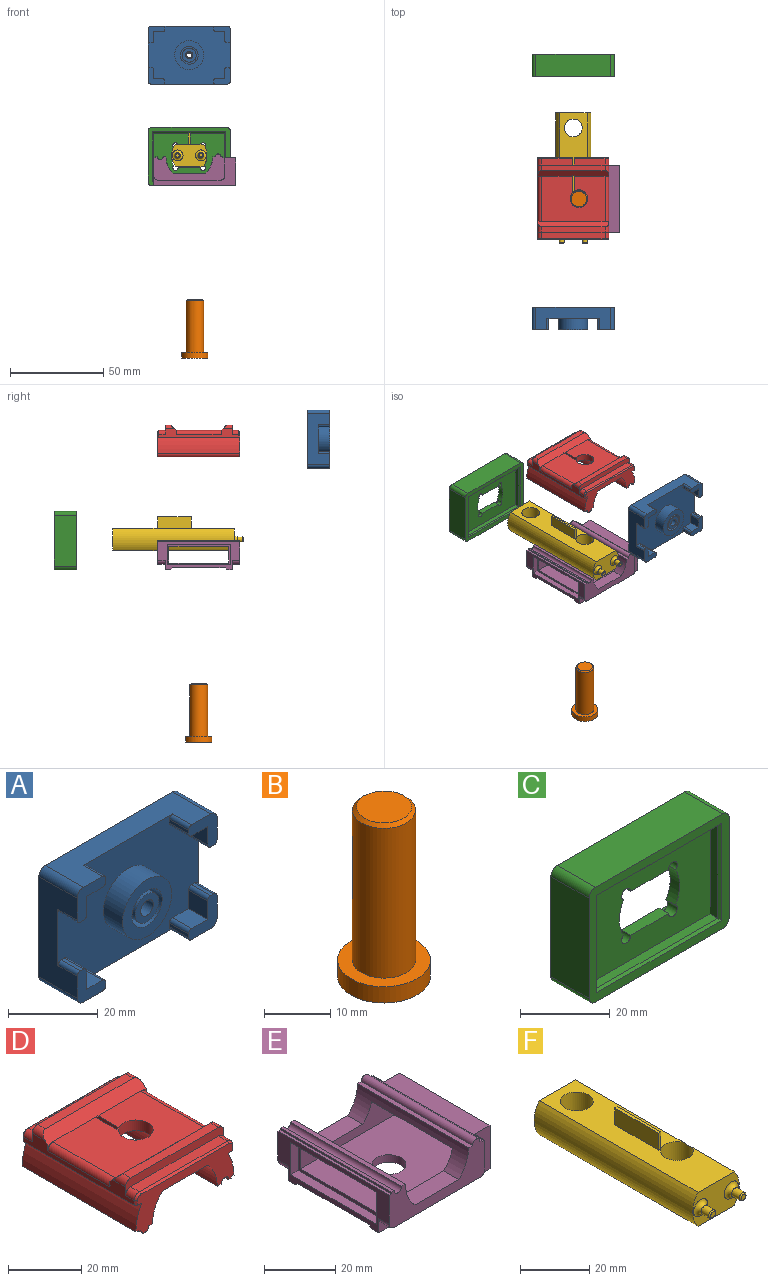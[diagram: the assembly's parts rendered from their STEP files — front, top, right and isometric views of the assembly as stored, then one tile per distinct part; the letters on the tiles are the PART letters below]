
ASSEMBLY  parts=6 mates=4
PART A: 69 faces, bbox 44.1x12x31.3 mm
  f0: plane 9.5x9.5mm, normal (0,-1,0), area 26.7mm2, adj f17,f39
  f1: plane 44.1x31.3mm, normal (0,-1,0), area 1015.1mm2, adj f10,f11,f12,f13,f19,f20,f21,f22
  f2: cylinder r=1.4mm len=2.8mm, axis (0,-1,0), area 17.6mm2, adj f5,f16
  f3: cylinder r=1.4mm len=2.8mm, axis (0,-1,0), area 17.6mm2, adj f5,f15
  f4: cylinder r=2mm len=6mm, axis (0,-1,0), area 75.4mm2, adj f18,f47
  f5: plane 38.1x25.3mm, normal (0,1,0), area 945.5mm2, adj f2,f3,f6,f7,f8,f9,f46
  f6: plane 25.3x2.4mm, normal (-1,0,0), area 60.7mm2, adj f5,f7,f9,f44
  f7: plane 38.1x2.4mm, normal (0,0,-1), area 91.4mm2, adj f5,f6,f8,f42
  f8: plane 25.3x2.4mm, normal (1,0,0), area 60.7mm2, adj f5,f7,f9,f43
  f9: plane 38.1x2.4mm, normal (0,0,1), area 91.4mm2, adj f5,f6,f8,f45
  f10: plane 27.3x12mm, normal (-1,0,0), area 235.8mm2, adj f1,f14,f28,f33,f48,f50,f58,f68
  f11: plane 40.1x12mm, normal (0,0,-1), area 312.6mm2, adj f1,f14,f33,f38,f50,f51,f55,f57
  f12: plane 27.3x12mm, normal (1,0,0), area 235.8mm2, adj f1,f14,f23,f38,f49,f51,f54,f64
  f13: plane 40.1x12mm, normal (0,0,1), area 312.6mm2, adj f1,f14,f23,f28,f48,f49,f61,f65
  f14: plane 44.1x31.3mm, normal (0,1,0), area 335.4mm2, adj f10,f11,f12,f13,f42,f43,f44,f45
  f15: plane 2.8x2.8mm, normal (0,1,0), area 6.2mm2, adj f3
  f16: plane 2.8x2.8mm, normal (0,1,0), area 6.2mm2, adj f2
  f17: cylinder r=3.75mm len=7.5mm, axis (0,1,0), area 141.4mm2, adj f0,f18
  f18: plane 7.5x7.5mm, normal (0,-1,0), area 31.6mm2, adj f4,f17
  f19: plane 6x1mm, normal (-1,0,0), area 6mm2, adj f1,f23,f61,f62
  f20: plane 6x5mm, normal (0,0,-1), area 30mm2, adj f1,f21,f23,f62
  f21: plane 6x5mm, normal (-1,0,0), area 30mm2, adj f1,f20,f23,f63
  f22: plane 6x1mm, normal (0,0,-1), area 6mm2, adj f1,f23,f63,f64
  f23: plane 9x9mm, normal (0,-1,0), area 43.3mm2, adj f12,f13,f19,f20,f21,f22,f49,f61
  f24: plane 6x1mm, normal (0,0,-1), area 6mm2, adj f1,f28,f67,f68
  f25: plane 6x5mm, normal (1,0,0), area 30mm2, adj f1,f26,f28,f67
  f26: plane 6x5mm, normal (0,0,-1), area 30mm2, adj f1,f25,f28,f66
  f27: plane 6x1mm, normal (1,0,0), area 6mm2, adj f1,f28,f65,f66
  f28: plane 9x9mm, normal (0,-1,0), area 43.3mm2, adj f10,f13,f24,f25,f26,f27,f48,f65
  f29: plane 6x1mm, normal (1,0,0), area 6mm2, adj f1,f33,f57,f60
  f30: plane 6x5mm, normal (0,0,1), area 30mm2, adj f1,f31,f33,f60
  f31: plane 6x5mm, normal (1,0,0), area 30mm2, adj f1,f30,f33,f59
  f32: plane 6x1mm, normal (0,0,1), area 6mm2, adj f1,f33,f58,f59
  f33: plane 9x9mm, normal (0,-1,0), area 43.3mm2, adj f10,f11,f29,f30,f31,f32,f50,f57
  f34: plane 6x5mm, normal (0,0,1), area 30mm2, adj f1,f37,f38,f56
  f35: plane 6x1mm, normal (-1,0,0), area 6mm2, adj f1,f38,f55,f56
  f36: plane 6x1mm, normal (0,0,1), area 6mm2, adj f1,f38,f53,f54
  f37: plane 6x5mm, normal (-1,0,0), area 30mm2, adj f1,f34,f38,f53
  f38: plane 9x9mm, normal (0,-1,0), area 43.3mm2, adj f11,f12,f34,f35,f36,f37,f51,f53
  f39: cylinder r=4.75mm len=9.5mm, axis (0,1,0), area 179.1mm2, adj f0,f41
  f40: cylinder r=7.75mm len=15.5mm, axis (0,1,0), area 292.2mm2, adj f1,f41
  f41: plane 15.5x15.5mm, normal (0,-1,0), area 117.8mm2, adj f39,f40
  f42: plane 39.3x0.6mm, normal (0,0.71,-0.71), area 32.8mm2, adj f7,f14,f43,f44
  f43: plane 26.5x0.6mm, normal (0.71,0.71,0), area 22mm2, adj f8,f14,f42,f45
  f44: plane 26.5x0.6mm, normal (-0.71,0.71,0), area 22mm2, adj f6,f14,f42,f45
  f45: plane 39.3x0.6mm, normal (0,0.71,0.71), area 32.8mm2, adj f9,f14,f43,f44
  f46: cylinder r=1.4mm len=2.8mm, axis (0,-1,0), area 22.9mm2, adj f5,f52
  f47: plane 4x4mm, normal (0,-1,0), area 2.4mm2, adj f4,f52
  f48: cylinder r=2mm len=12mm, axis (0,1,0), area 37.7mm2, adj f10,f13,f14,f28
  f49: cylinder r=2mm len=12mm, axis (0,-1,0), area 37.7mm2, adj f12,f13,f14,f23
  f50: cylinder r=2mm len=12mm, axis (0,-1,0), area 37.7mm2, adj f10,f11,f14,f33
  f51: cylinder r=2mm len=12mm, axis (0,1,0), area 37.7mm2, adj f11,f12,f14,f38
  f52: cone r=1.4mm half-angle=45deg, axis (0,-1,0), area 5.7mm2, adj f46,f47
  f53: cylinder r=1mm len=6mm, axis (0,-1,0), area 9.4mm2, adj f1,f36,f37,f38
  f54: cylinder r=1mm len=6mm, axis (0,-1,0), area 9.4mm2, adj f1,f12,f36,f38
  f55: cylinder r=1mm len=6mm, axis (0,-1,0), area 9.4mm2, adj f1,f11,f35,f38
  f56: cylinder r=1mm len=6mm, axis (0,-1,0), area 9.4mm2, adj f1,f34,f35,f38
  f57: cylinder r=1mm len=6mm, axis (0,1,0), area 9.4mm2, adj f1,f11,f29,f33
  f58: cylinder r=1mm len=6mm, axis (0,1,0), area 9.4mm2, adj f1,f10,f32,f33
  f59: cylinder r=1mm len=6mm, axis (0,1,0), area 9.4mm2, adj f1,f31,f32,f33
  f60: cylinder r=1mm len=6mm, axis (0,1,0), area 9.4mm2, adj f1,f29,f30,f33
  f61: cylinder r=1mm len=6mm, axis (0,1,0), area 9.4mm2, adj f1,f13,f19,f23
  f62: cylinder r=1mm len=6mm, axis (0,1,0), area 9.4mm2, adj f1,f19,f20,f23
  f63: cylinder r=1mm len=6mm, axis (0,1,0), area 9.4mm2, adj f1,f21,f22,f23
  f64: cylinder r=1mm len=6mm, axis (0,1,0), area 9.4mm2, adj f1,f12,f22,f23
  f65: cylinder r=1mm len=6mm, axis (0,-1,0), area 9.4mm2, adj f1,f13,f27,f28
  f66: cylinder r=1mm len=6mm, axis (0,-1,0), area 9.4mm2, adj f1,f26,f27,f28
  f67: cylinder r=1mm len=6mm, axis (0,-1,0), area 9.4mm2, adj f1,f24,f25,f28
  f68: cylinder r=1mm len=6mm, axis (0,-1,0), area 9.4mm2, adj f1,f10,f24,f28
PART B: 6 faces, bbox 14x14x31.2 mm
  f0: cylinder r=4.75mm len=27.6mm, axis (0,0,-1), area 823.7mm2, adj f3,f5
  f1: plane 8.3x8.3mm, normal (0,0,1), area 54.1mm2, adj f5
  f2: cylinder r=7mm len=14mm, axis (0,0,-1), area 131.9mm2, adj f3,f4
  f3: plane 14x14mm, normal (0,0,1), area 83.1mm2, adj f0,f2
  f4: plane 14x14mm, normal (0,0,-1), area 153.9mm2, adj f2
  f5: cone r=4.15mm half-angle=45deg, axis (0,0,-1), area 23.7mm2, adj f0,f1
PART C: 32 faces, bbox 44.1x12x31.3 mm
  f0: plane 38.1x25.3mm, normal (0,1,0), area 736.2mm2, adj f1,f2,f3,f4,f5,f6,f7,f8
  f1: cylinder r=1.4mm len=3mm, axis (0,1,0), area 17.2mm2, adj f0,f2,f8,f9
  f2: plane 11.93x3mm, normal (0,0,-1), area 35.8mm2, adj f0,f1,f3,f9
  f3: cylinder r=1.4mm len=3mm, axis (0,1,0), area 17.2mm2, adj f0,f2,f4,f9
  f4: cylinder r=9.5mm len=9.7mm, axis (0,1,0), area 30.6mm2, adj f0,f3,f5,f9
  f5: cylinder r=1.4mm len=3mm, axis (0,1,0), area 17.2mm2, adj f0,f4,f6,f9
  f6: plane 11.93x3mm, normal (0,0,1), area 35.8mm2, adj f0,f5,f7,f9
  f7: cylinder r=1.4mm len=3mm, axis (0,1,0), area 17.2mm2, adj f0,f6,f8,f9
  f8: cylinder r=9.5mm len=9.7mm, axis (0,1,0), area 30.6mm2, adj f0,f1,f7,f9
  f9: plane 38.1x25.3mm, normal (0,-1,0), area 736.2mm2, adj f1,f2,f3,f4,f5,f6,f7,f8
  f10: plane 38.1x2.4mm, normal (0,0,-1), area 91.4mm2, adj f9,f11,f13,f25
  f11: plane 25.3x2.4mm, normal (1,0,0), area 60.7mm2, adj f9,f10,f12,f24
  f12: plane 38.1x2.4mm, normal (0,0,1), area 91.4mm2, adj f9,f11,f13,f26
  f13: plane 25.3x2.4mm, normal (-1,0,0), area 60.7mm2, adj f9,f10,f12,f27
  f14: plane 40.1x12mm, normal (0,0,1), area 481.2mm2, adj f18,f23,f28,f31
  f15: plane 27.3x12mm, normal (-1,0,0), area 327.6mm2, adj f18,f23,f28,f29
  f16: plane 40.1x12mm, normal (0,0,-1), area 481.2mm2, adj f18,f23,f29,f30
  f17: plane 27.3x12mm, normal (1,0,0), area 327.6mm2, adj f18,f23,f30,f31
  f18: plane 44.1x31.3mm, normal (0,-1,0), area 335.4mm2, adj f14,f15,f16,f17,f24,f25,f26,f27
  f19: plane 25.3x6mm, normal (1,0,0), area 151.8mm2, adj f0,f20,f22,f23
  f20: plane 38.1x6mm, normal (0,0,-1), area 228.6mm2, adj f0,f19,f21,f23
  f21: plane 25.3x6mm, normal (-1,0,0), area 151.8mm2, adj f0,f20,f22,f23
  f22: plane 38.1x6mm, normal (0,0,1), area 228.6mm2, adj f0,f19,f21,f23
  f23: plane 44.1x31.3mm, normal (0,1,0), area 413mm2, adj f14,f15,f16,f17,f19,f20,f21,f22
  f24: plane 26.5x0.6mm, normal (0.71,-0.71,0), area 22mm2, adj f11,f18,f25,f26
  f25: plane 39.3x0.6mm, normal (0,-0.71,-0.71), area 32.8mm2, adj f10,f18,f24,f27
  f26: plane 39.3x0.6mm, normal (0,-0.71,0.71), area 32.8mm2, adj f12,f18,f24,f27
  f27: plane 26.5x0.6mm, normal (-0.71,-0.71,0), area 22mm2, adj f13,f18,f25,f26
  f28: cylinder r=2mm len=12mm, axis (0,-1,0), area 37.7mm2, adj f14,f15,f18,f23
  f29: cylinder r=2mm len=12mm, axis (0,1,0), area 37.7mm2, adj f15,f16,f18,f23
  f30: cylinder r=2mm len=12mm, axis (0,-1,0), area 37.7mm2, adj f16,f17,f18,f23
  f31: cylinder r=2mm len=12mm, axis (0,1,0), area 37.7mm2, adj f14,f17,f18,f23
PART D: 62 faces, bbox 38x44x17 mm
  f0: plane 1.9x1.36mm, normal (0,1,0), area 0.7mm2, adj f18,f42,f61
  f1: plane 1.9x1.36mm, normal (0,-1,0), area 0.7mm2, adj f17,f41,f60
  f2: plane 16.5x3.4mm, normal (0,0,1), area 56.1mm2, adj f4,f36,f40,f49
  f3: plane 16.5x3.4mm, normal (0,0,1), area 56.1mm2, adj f5,f36,f39,f52
  f4: plane 18x3.6mm, normal (1,0,0), area 64.1mm2, adj f2,f6,f8,f30,f31,f35,f36,f49
  f5: plane 17.96x3.6mm, normal (-1,0,0), area 63.9mm2, adj f3,f6,f8,f9,f10,f35,f36,f52
  f6: plane 34x24.21mm, normal (0,0,1), area 744.1mm2, adj f4,f5,f10,f31,f41,f42,f60,f61
  f7: plane 34x3.4mm, normal (0,0,1), area 115.6mm2, adj f34,f47,f48,f57
  f8: plane 44x17.35mm, normal (0,0,-1), area 674.5mm2, adj f4,f5,f9,f10,f26,f27,f29,f30
  f9: plane 18.49x12mm, normal (0,1,0), area 111.8mm2, adj f5,f8,f11,f12,f13,f14,f15,f16
  f10: cylinder r=4.75mm len=9.5mm, axis (0,0,-1), area 107.3mm2, adj f5,f6,f8,f31
  f11: cylinder r=1.5mm len=44mm, axis (0,1,0), area 207.3mm2, adj f9,f12,f28,f29
  f12: plane 44x1mm, normal (0,0,-1), area 44mm2, adj f9,f11,f13,f29
  f13: plane 44x0.5mm, normal (1,0,0), area 22mm2, adj f9,f12,f14,f29
  f14: plane 44x0.99mm, normal (0,0,-1), area 43.7mm2, adj f9,f13,f15,f29
  f15: cylinder r=19mm len=44mm, axis (0,1,0), area 390.5mm2, adj f9,f14,f16,f29
  f16: plane 44x2.27mm, normal (0,0,-1), area 99.4mm2, adj f9,f15,f17,f29,f54,f55
  f17: plane 42.8x4.5mm, normal (1,0,0), area 102.4mm2, adj f1,f16,f32,f34,f36,f39,f41,f44
  f18: plane 42.8x4.5mm, normal (-1,0,0), area 102.4mm2, adj f0,f19,f34,f36,f38,f40,f42,f43
  f19: plane 44x2.27mm, normal (0,0,-1), area 99.4mm2, adj f18,f20,f29,f30,f51,f59
  f20: cylinder r=19mm len=44mm, axis (0,1,0), area 390.5mm2, adj f19,f21,f29,f30
  f21: plane 44x0.99mm, normal (0,0,-1), area 43.7mm2, adj f20,f22,f29,f30
  f22: plane 44x0.5mm, normal (-1,0,0), area 22mm2, adj f21,f23,f29,f30
  f23: plane 44x1mm, normal (0,0,-1), area 44mm2, adj f22,f24,f29,f30
  f24: cylinder r=1.5mm len=44mm, axis (0,1,0), area 207.3mm2, adj f23,f25,f29,f30
  f25: plane 44x1.5mm, normal (0,0,-1), area 66mm2, adj f24,f26,f29,f30
  f26: cylinder r=12.5mm len=44mm, axis (0,1,0), area 442.1mm2, adj f8,f25,f29,f30
  f27: cylinder r=12.5mm len=44mm, axis (0,1,0), area 442.1mm2, adj f8,f9,f28,f29
  f28: plane 44x1.5mm, normal (0,0,-1), area 66mm2, adj f9,f11,f27,f29
  f29: plane 37.99x13.5mm, normal (0,-1,0), area 233.8mm2, adj f8,f11,f12,f13,f14,f15,f16,f19
  f30: plane 18.49x13.5mm, normal (0,1,0), area 118.9mm2, adj f4,f8,f19,f20,f21,f22,f23,f24
  f31: plane 3.6x0.94mm, normal (0,1,0), area 3.4mm2, adj f4,f6,f8,f10
  f32: plane 1.9x1.36mm, normal (0,1,0), area 0.7mm2, adj f17,f41,f61
  f33: plane 34x3mm, normal (0,0,1), area 102mm2, adj f34,f45,f46,f61
  f34: plane 38x4.9mm, normal (0,-1,0), area 110.1mm2, adj f7,f17,f18,f33,f45,f46,f47,f48
  f35: plane 6x1mm, normal (0,0,-1), area 6mm2, adj f4,f5,f36,f60
  f36: plane 38x4.9mm, normal (0,1,0), area 110.2mm2, adj f2,f3,f4,f5,f17,f18,f35,f37
  f37: plane 34x3mm, normal (0,0,1), area 102mm2, adj f36,f43,f44,f60
  f38: plane 1.9x1.36mm, normal (0,-1,0), area 0.7mm2, adj f18,f42,f60
  f39: cylinder r=2mm len=3.4mm, axis (0,1,0), area 10.7mm2, adj f3,f17,f36,f53
  f40: cylinder r=2mm len=3.4mm, axis (0,-1,0), area 10.7mm2, adj f2,f18,f36,f50
  f41: cylinder r=2mm len=24.21mm, axis (0,1,0), area 75.5mm2, adj f1,f6,f17,f32,f60,f61
  f42: cylinder r=2mm len=24.21mm, axis (0,-1,0), area 75.5mm2, adj f0,f6,f18,f38,f60,f61
  f43: cylinder r=2mm len=5mm, axis (0,-1,0), area 11.7mm2, adj f18,f36,f37,f60
  f44: cylinder r=2mm len=5mm, axis (0,1,0), area 11.7mm2, adj f17,f36,f37,f60
  f45: cylinder r=2mm len=5mm, axis (0,-1,0), area 11.7mm2, adj f18,f33,f34,f61
  f46: cylinder r=2mm len=5mm, axis (0,1,0), area 11.7mm2, adj f17,f33,f34,f61
  f47: cylinder r=2mm len=3.4mm, axis (0,-1,0), area 10.7mm2, adj f7,f18,f34,f58
  f48: cylinder r=2mm len=3.4mm, axis (0,1,0), area 10.7mm2, adj f7,f17,f34,f56
  f49: plane 16.5x0.6mm, normal (0,0.71,0.71), area 14mm2, adj f2,f4,f30,f50
  f50: cone r=1.4mm half-angle=45deg, axis (0,-1,0), area 2.3mm2, adj f30,f40,f49,f51
  f51: plane 1.6x0.6mm, normal (-0.71,0.71,0), area 1.4mm2, adj f18,f19,f30,f50
  f52: plane 16.5x0.6mm, normal (0,0.71,0.71), area 14mm2, adj f3,f5,f9,f53
  f53: cone r=1.4mm half-angle=45deg, axis (0,-1,0), area 2.3mm2, adj f9,f39,f52,f54
  f54: plane 1.6x0.6mm, normal (0.71,0.71,0), area 1.4mm2, adj f9,f16,f17,f53
  f55: plane 1.6x0.6mm, normal (0.71,-0.71,0), area 1.4mm2, adj f16,f17,f29,f56
  f56: cone r=1.4mm half-angle=45deg, axis (0,1,0), area 2.3mm2, adj f29,f48,f55,f57
  f57: plane 34x0.6mm, normal (0,-0.71,0.71), area 28.8mm2, adj f7,f29,f56,f58
  f58: cone r=1.4mm half-angle=45deg, axis (0,1,0), area 2.3mm2, adj f29,f47,f57,f59
  f59: plane 1.6x0.6mm, normal (-0.71,-0.71,0), area 1.4mm2, adj f18,f19,f29,f58
  f60: plane 38x3mm, normal (0,-0.71,0.71), area 153.8mm2, adj f1,f4,f5,f6,f17,f18,f35,f37
  f61: plane 38x3mm, normal (0,0.71,0.71), area 153.7mm2, adj f0,f6,f17,f18,f32,f33,f41,f42
PART E: 49 faces, bbox 44x44x17 mm
  f0: plane 38x14mm, normal (0,1,0), area 268.4mm2, adj f3,f5,f11,f12,f13,f17,f18,f19
  f1: plane 38x14mm, normal (0,-1,0), area 268.4mm2, adj f3,f4,f5,f11,f12,f16,f17,f18
  f2: plane 36x14.9mm, normal (1,0,0), area 136.3mm2, adj f3,f15,f26,f27,f28,f29,f30,f31
  f3: plane 44x7mm, normal (0,0,1), area 260mm2, adj f0,f1,f2,f22,f26,f28,f43,f44
  f4: plane 34x4mm, normal (0,0,-1), area 136mm2, adj f1,f28,f46,f48
  f5: plane 44x14.9mm, normal (-1,0,0), area 215.5mm2, adj f0,f1,f15,f21,f26,f27,f28,f29
  f6: plane 38x9mm, normal (0,1,0), area 212.6mm2, adj f8,f9,f10,f11,f12,f16,f34,f39
  f7: plane 38x9mm, normal (0,-1,0), area 212.6mm2, adj f8,f9,f10,f11,f12,f13,f34,f39
  f8: plane 38x32mm, normal (0,0,1), area 1145.1mm2, adj f6,f7,f14,f34,f39
  f9: plane 32x3.87mm, normal (0,0,-1), area 123.7mm2, adj f6,f7,f12,f39
  f10: plane 32x9.87mm, normal (0,0,-1), area 315.7mm2, adj f6,f7,f11,f34
  f11: cylinder r=12.5mm len=44mm, axis (0,1,0), area 217.5mm2, adj f0,f1,f6,f7,f10,f13,f16,f25
  f12: cylinder r=12.5mm len=44mm, axis (0,1,0), area 217.5mm2, adj f0,f1,f6,f7,f9,f13,f16,f17
  f13: plane 17.35x6mm, normal (0,0,1), area 104.1mm2, adj f0,f7,f11,f12
  f14: cylinder r=4.75mm len=9.5mm, axis (0,0,1), area 77.7mm2, adj f8,f15
  f15: plane 44x28.21mm, normal (0,0,-1), area 1170.2mm2, adj f2,f5,f14,f41,f42
  f16: plane 17.35x6mm, normal (0,0,1), area 104.1mm2, adj f1,f6,f11,f12
  f17: plane 44x1.5mm, normal (0,0,1), area 66mm2, adj f0,f1,f12,f18
  f18: cylinder r=1.5mm len=44mm, axis (0,1,0), area 207.3mm2, adj f0,f1,f17,f19
  f19: plane 44x1mm, normal (0,0,1), area 44mm2, adj f0,f1,f18,f20
  f20: plane 44x0.6mm, normal (-1,0,0), area 26.4mm2, adj f0,f1,f19,f21
  f21: plane 44x1mm, normal (0,0,1), area 44mm2, adj f0,f1,f5,f20
  f22: plane 44x0.6mm, normal (1,0,0), area 26.4mm2, adj f0,f1,f3,f23
  f23: plane 44x1mm, normal (0,0,1), area 44mm2, adj f0,f1,f22,f24
  f24: cylinder r=1.5mm len=44mm, axis (0,1,0), area 207.3mm2, adj f0,f1,f23,f25
  f25: plane 44x1.5mm, normal (0,0,1), area 66mm2, adj f0,f1,f11,f24
  f26: plane 44x14.9mm, normal (0,1,0), area 205.1mm2, adj f2,f3,f5,f27,f40,f44,f45,f47
  f27: plane 44x3mm, normal (0,0,-1), area 132mm2, adj f2,f5,f26,f42
  f28: plane 44x14.9mm, normal (0,-1,0), area 205.1mm2, adj f2,f3,f4,f5,f29,f43,f46,f48
  f29: plane 44x3mm, normal (0,0,-1), area 132mm2, adj f2,f5,f28,f41
  f30: plane 11x3mm, normal (0,1,0), area 33mm2, adj f2,f31,f33,f34
  f31: plane 34x3mm, normal (0,0,1), area 102mm2, adj f2,f30,f32,f34
  f32: plane 11x3mm, normal (0,-1,0), area 33mm2, adj f2,f31,f33,f34
  f33: plane 34x3mm, normal (0,0,-1), area 102mm2, adj f2,f30,f32,f34
  f34: plane 34x11mm, normal (1,0,0), area 86mm2, adj f6,f7,f8,f10,f30,f31,f32,f33
  f35: plane 11x3mm, normal (0,-1,0), area 33mm2, adj f5,f36,f38,f39
  f36: plane 34x3mm, normal (0,0,1), area 102mm2, adj f5,f35,f37,f39
  f37: plane 11x3mm, normal (0,1,0), area 33mm2, adj f5,f36,f38,f39
  f38: plane 34x3mm, normal (0,0,-1), area 102mm2, adj f5,f35,f37,f39
  f39: plane 34x11mm, normal (-1,0,0), area 86mm2, adj f6,f7,f8,f9,f35,f36,f37,f38
  f40: plane 34x4mm, normal (0,0,-1), area 136mm2, adj f0,f26,f45,f47
  f41: plane 44x0.9mm, normal (0,0.71,-0.71), area 55.8mm2, adj f2,f5,f15,f29
  f42: plane 44x0.9mm, normal (0,-0.71,-0.71), area 55.8mm2, adj f2,f5,f15,f27
  f43: plane 9.9x4mm, normal (1,0,0), area 39.6mm2, adj f1,f3,f28,f46
  f44: plane 9.9x4mm, normal (1,0,0), area 39.6mm2, adj f0,f3,f26,f45
  f45: cylinder r=2mm len=4mm, axis (0,-1,0), area 12.6mm2, adj f0,f26,f40,f44
  f46: cylinder r=2mm len=4mm, axis (0,-1,0), area 12.6mm2, adj f1,f4,f28,f43
  f47: cylinder r=2mm len=4mm, axis (0,-1,0), area 12.6mm2, adj f0,f5,f26,f40
  f48: cylinder r=2mm len=4mm, axis (0,-1,0), area 12.6mm2, adj f1,f4,f5,f28
PART F: 21 faces, bbox 21.1x70x18 mm
  f0: plane 65x14.73mm, normal (0,0,1), area 798.8mm2, adj f1,f2,f4,f5,f6,f7,f8,f14
  f1: cylinder r=9.5mm len=65mm, axis (0,1,0), area 841.1mm2, adj f0,f3,f4,f5,f14
  f2: cylinder r=9.5mm len=65mm, axis (0,1,0), area 844.2mm2, adj f0,f3,f4,f5
  f3: plane 65x14.73mm, normal (0,0,-1), area 816.7mm2, adj f1,f2,f4,f5,f14,f15
  f4: plane 19x12mm, normal (0,-1,0), area 158.9mm2, adj f0,f1,f2,f3,f19,f20
  f5: plane 19x12mm, normal (0,1,0), area 211.8mm2, adj f0,f1,f2,f3
  f6: plane 6x1mm, normal (0,1,0), area 6mm2, adj f0,f7,f8,f9
  f7: plane 17.96x6mm, normal (-1,0,0), area 107.8mm2, adj f0,f6,f9,f16
  f8: plane 17.96x6mm, normal (1,0,0), area 107.8mm2, adj f0,f6,f9,f16
  f9: plane 17.96x1mm, normal (0,0,1), area 18mm2, adj f6,f7,f8,f16
  f10: cylinder r=1.4mm len=3.1mm, axis (0,1,0), area 27.3mm2, adj f18,f20
  f11: plane 2x2mm, normal (0,-1,0), area 3.1mm2, adj f18
  f12: cylinder r=1.4mm len=3.1mm, axis (0,1,0), area 27.3mm2, adj f17,f19
  f13: plane 2x2mm, normal (0,-1,0), area 3.1mm2, adj f17
  f14: cylinder r=4.75mm len=12mm, axis (0,0,-1), area 355.6mm2, adj f0,f1,f3
  f15: cylinder r=4.75mm len=12mm, axis (0,0,1), area 358.1mm2, adj f0,f3
  f16: plane 6x1mm, normal (0,-1,0), area 6mm2, adj f0,f7,f8,f9
  f17: cone r=1mm half-angle=45deg, axis (0,1,0), area 4.3mm2, adj f12,f13
  f18: cone r=1mm half-angle=45deg, axis (0,1,0), area 4.3mm2, adj f10,f11
  f19: torus R=2.9mm, axis (0,-1,0), area 28.8mm2, adj f4,f12
  f20: torus R=2.9mm, axis (0,-1,0), area 28.8mm2, adj f4,f10
PLACE A rot(axis=(0.48,0,0.88),0deg) t=(-0.17,-64.41,66.2)mm
PLACE B t=(2.88,-0.12,-96.02)mm
PLACE C t=(-0.17,71.4,11.85)mm
PLACE D rot(axis=(-0.27,0,-0.96),0deg) t=(-0.12,-0.12,58.29)mm
PLACE E t=(-0.12,-0.12,11.81)mm
PLACE F t=(-0.12,-0.12,12.56)mm fixed
MATE slider B.f0 <-> F.f14  axis (0,0,-1) through (2.88,-0.12,-65.42)mm
MATE slider D.f10 <-> B.f0  axis (0,0,-1) through (2.88,-0.12,67.29)mm
MATE parallel D.f7 <-> F.f0  axis (0,0,1) through (-0.12,-19.82,70.89)mm
MATE planar D.f17 <-> A.f6  axis (1,0,0) through (18.88,-0.12,68.82)mm
